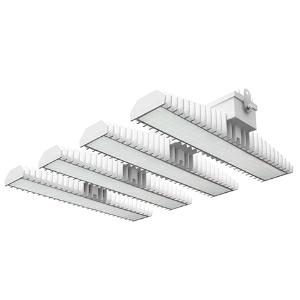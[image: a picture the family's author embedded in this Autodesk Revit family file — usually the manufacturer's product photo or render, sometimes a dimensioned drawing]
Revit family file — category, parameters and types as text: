
# Revit family: 3f_filippi_-_3f_lem_ht_ampio_3f_filippi_-_59028_a0812_-_3f_lem_4_ht_led_120_cr_ampio___vs_1431
name_source: partatom
category: Lighting Fixtures
units: mm (PartAtom-declared; Revit-internal decimal feet)

## family parameters
Cut with Voids When Loaded = No
Host = Face
Light Source = No
Part Type = Normal
Room Calculation Point = No
Round Connector Dimension = Use Diameter
Shared = No

## types (1)
- 3F Filippi - 3F LEM HT Ampio (1 x LED, 17036 lm, 136 W, 4000 K)
    Apparent Load = 136 VA
    Approval mark = ENEC
    CIE Flux Codes = 67 90 97 100 100
    Color Rendering = 80
    Color Temperature = 4000 K
    Control Gear = Electronic ballast
    Default Elevation = 1800 mm
    Description = Industrial luminaire with high light output and high luminous efficiency designed with the most innovative technologies for environments with temperature up to 70°C.

ILLUMINOTECHNICAL
Luminous efficiency 100% (DLOR 98%, ULOR 2%).
Initial luminous flux of the luminaire 17036 lm.
Direct symmetric wide distribution: the illuminated area has a rectangular shape.
Installation Interdistance Transv.D = 1.24 x hu - Long.D = 1.20 x hu.
Tabular UGR (CIE 117 - 4H-8H; S=0.25H; 70/50/20): RUG 21.3 - 21.4.
Beam angle: 82° - 83°.
Luminous efficacy 125 lm/W.
Lifetime (L93/B10): 30000 h. (tq+25°C)
Lifetime (L90/B10): 50000 h. (tq+25°C)
Lifetime (L85/B10): 80000 h. (tq+25°C)
Lifetime (L80/B10): 100000 h. (tq+25°C)
Lifetime (L85/B10): 50000 h. (tq+70°C)
Sudden decreased luminous flux after 50000 hours: 0% (C0).
Photobiological safety in compliance with IEC/TR 62778: RG0 risk exempt, (IEC 62471).
In compliance with IEC/EN 62722-2-1 - IEC/EN 62717 standards.
Luminous flux at +70°C: -13.5%.

SOURCE
4 Mid-Power linear LED modules 30W/840.
Energy efficiency class (UE 2019/2020 - UE 2019/2015): C.
CIE 13.3 Colour rendering index: CRI >80 (R9 <50%).
IES TM-30 Fidelity Index: Rf = 84 Rg = 95.
CCT nominal colour temperature 4000 K.
Colour initial tolerance (MacAdam): SDCM 3.

MECHANICAL
Passive modular heatsinks in die-casted aluminium, painted in white colour.
To optimize the thermal management of the LED module, the heatsinks are oversized and provided with self-cleaning of cooling fins.
Wiring body in aluminium and galvanised steel anchored solidly to the sinks and thermally separated.
3F Lens lenses with high luminous efficiency, transparent polycarbonate, fixed to the LED modules.
Fixing brackets in stainless steel.
Luminaire with limited surface temperature. - D - (EN 60598-2-24)
Dimensions: 757x542 mm, height 133 mm. Weight 19.225 kg.
IP65 protection degree.
Mechanical strength to impacts IK08 (5 joule).
Glow-wire test resistance 850°C.

ELECTRICAL
Halogen Free electronic wiring 230V-50/60Hz, power factor 0.97, THD <25%, constant output current, class I, 2 driver.
Power of the luminaire 136 W.
CE - IEC 60598-1 - EN 60598-1.
SAFE FLICKER: PstLM=<1 and SVM=<0.4 (IEC TR 61547-1 and IEC TR 63158), to ensure a more comfortable and safe light.
Luminaire compliant with EN 60598-2-22 for power supply from a centralised emergency system CPSS (Central Power Supply System), not incorporated in the luminaire - high risk areas excluded. The default power and flux are 100% in AC and 100% in DC.
Ambient temperature from -30°C to +70°C.
Temperature class T6 max 85°C.
Quick connection via M20 3P connector with 9-13 mm tightening range.
Power unit positioned on a separate compartment by the LED module to ensure optimum temperatures of cabling components, to be inspectable and maintainable.
Relative humidity UR: <85%.

INSTALLATION
Ceiling / Suspended / Wall.
All accessories dedicated to this product are available on the Catalog and on our website www.3F-Filippi.com.

ACCESSORIES
A0812 - Anti-glare microprismatic VS moulded glass, tempered, not flammable, with sealing gasket.
One required for each light module. The pack contains 10 pieces.

APPLICATIONS
In commercial environments, exhibition and industrial areas, stores, open areas.
Applications with high ambient temperature up to 70°C.

WARNING
Fixture not suitable for cold stores with an ambient temperature <0°C and/or relative humidity >85%.
Luminaire designed for disposal/recycling at end-of-life.
Replaceable (LED only) light source by a professional. Replaceable control gear by a professional.
    Height = 133 mm  [stored 0.436352 ft]
    Lamp = 1 x LED
    Lamp Light Flux = 17036 lm
    Lamp Power = 136 W
    Lamp count = 1
    Length = 757 mm
    Lifetime = 50000 h
    Luminous efficacy = 125 lm/W
    Manufacturer = 3F Filippi
    ModVariant = No
    Model = 3F Filippi - 59028+A0812 - 3F LEM 4 HT LED 120 CR AMPIO + VS
    Mounting Place = Ceiling
    Mounting Type = Pendant
    Number of Poles = 1
    OnlyDefault = Yes
    Power Factor = 1
    Product Name = 3F Filippi - 3F LEM HT Ampio
    Product group = pendant luminaire
    ProductGroupID = 9
    Protection Class = Protection class I
    Protection Degree = IP 65
    RLX_Detail_Level = 1
    RLX_Emergency_Light_Flux = 0 lm
    RLX_Emergency_Type = 0
    RLX_Emergency_Type_DB = No
    RlxData = <blob elided: 119373 chars, md5=2a9e54ae>
    Socket = socket
    Standby Power = 0 W
    System Light Flux = 17036 lm
    System Power = 136 W
    Type Comments = Product without accessories
    Type Image = 3f_filippi_-_lem_4__a0812.jpg
    URL = http://relux.com
    VarID = ---
    Voltage = 0 V
    Weight = 0.00 kg
    Width = 542 mm

note: [stored X ft] marks values corroborated as IEEE doubles in the binary element streams (Revit-internal decimal feet)

## geometry (parser evidence)
native form markers: Blend x4, Sweep x12
no freeform markers — native parametric forms only
